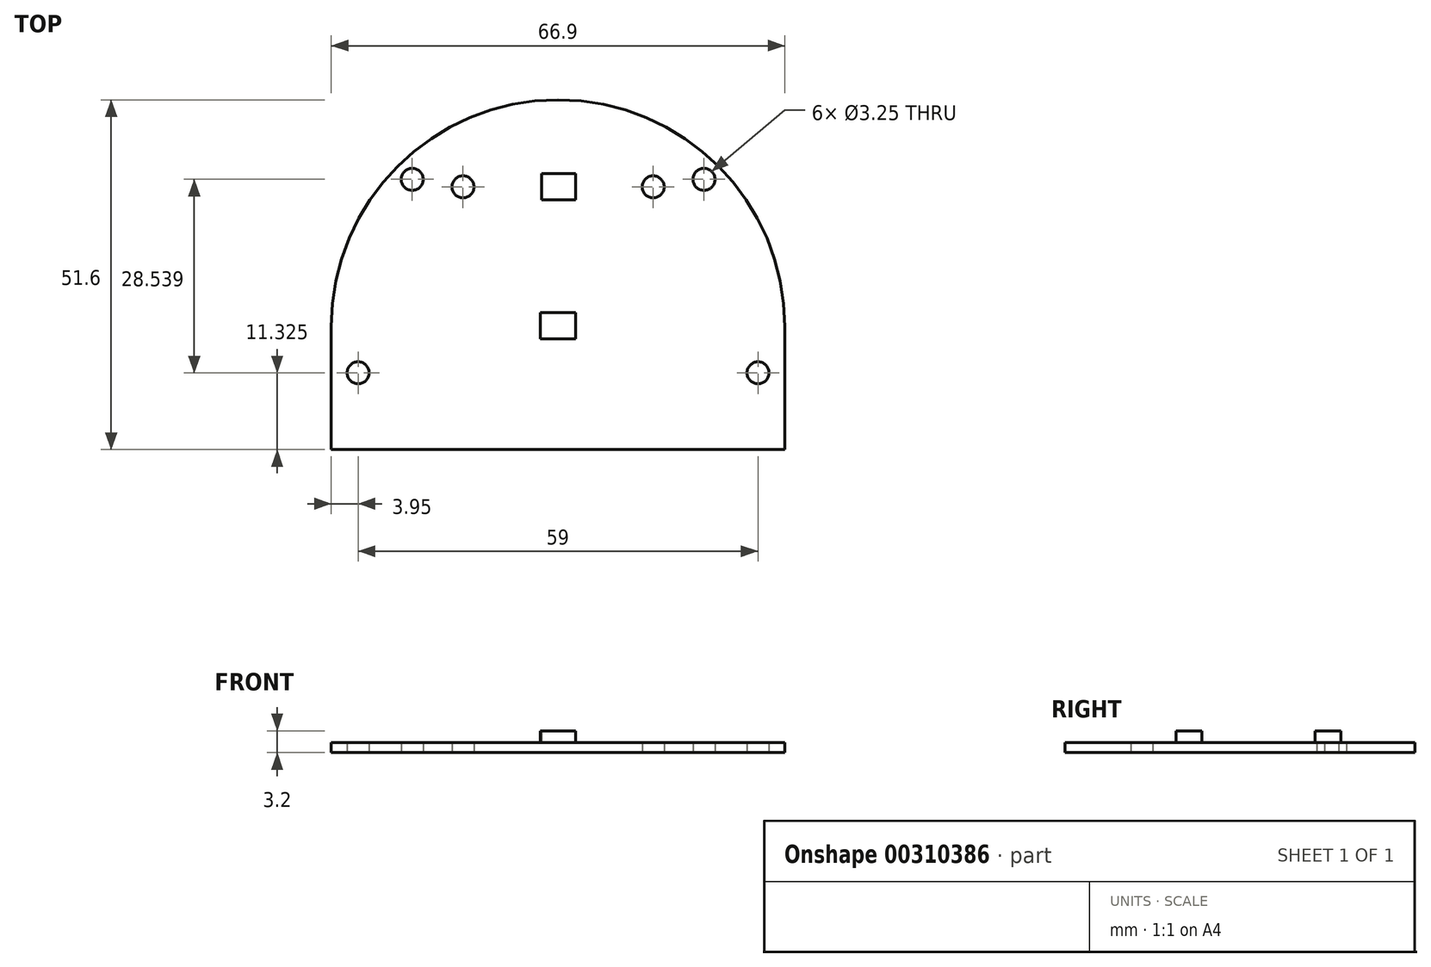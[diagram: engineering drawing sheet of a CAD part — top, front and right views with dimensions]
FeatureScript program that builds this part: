
annotation { "Feature Type Name" : "Feature", "Feature Type Description" : "" }
export const myFeature = defineFeature(function(context is Context, id is Id, definition is map)
    precondition{}
    {
        {
            var Q0;
            Q0=qCreatedBy(makeId("Top.planeOp"),FACE);
            var sketch = newSketch(context, id + "F0", { "sketchPlane" : qUnion([Q0])});
            skLineSegment(sketch, "E0.bottom", {"start": v(-33.45, 25.8) * mm, "end": v(33.45, 25.8) * mm});
            skLineSegment(sketch, "E0.top", {"start": v(-33.45, -25.8) * mm, "end": v(33.45, -25.8) * mm});
            skLineSegment(sketch, "E0.left", {"start": v(-33.45, 25.8) * mm, "end": v(-33.45, -25.8) * mm});
            skLineSegment(sketch, "E0.right", {"start": v(33.45, 25.8) * mm, "end": v(33.45, -25.8) * mm});
            skPoint(sketch, "E0.middle", {"position": v(0, 0) * mm});
            skSolve(sketch);
        }
        {
            var Q0;
            Q0=makeQuery(id+"F0.imprint","IMPRINT",FACE,{"disambiguationData":[TD([[makeQuery(id+"F0.imprint","IMPRINT",EDGE,{"derivedFrom":sQuery(id+"F0.wireOp",EDGE,"E0.bottom")}),-1.0]])]});
            extrude(context, id + "F1", {"entities" : qUnion([Q0]), "depth" : 1.5 * mm});
        }
        {
            var Q0;
            Q0=makeQuery(id+"F1.opExtrude","SWEPT_EDGE",EDGE,{"disambiguationData":[OSD([sQuery(id+"F0.wireOp",EDGE,"E0.bottom"),sQuery(id+"F0.wireOp",EDGE,"E0.left")])]});
            var Q1;
            Q1=makeQuery(id+"F1.opExtrude","SWEPT_EDGE",EDGE,{"disambiguationData":[OSD([sQuery(id+"F0.wireOp",EDGE,"E0.bottom"),sQuery(id+"F0.wireOp",EDGE,"E0.right")])]});
            fillet(context, id + "F2", {"entities" : qUnion([Q0, Q1]), "radius" : 33.45 * mm, "tangentPropagation" : true, "allowEdgeOverflow" : false});
        }
        {
            var Q0;
            Q0=qCreatedBy(makeId("Top.planeOp"),FACE);
            var sketch = newSketch(context, id + "F3", { "sketchPlane" : qUnion([Q0])});
            skCircle(sketch, "E1", {"center": v(-21.53, 14.06) * mm, "radius": 1.63 * mm});
            skCircle(sketch, "E2", {"center": v(-14.02, 12.95) * mm, "radius": 1.63 * mm});
            skCircle(sketch, "E3", {"center": v(21.53, 14.06) * mm, "radius": 1.63 * mm});
            skCircle(sketch, "E4", {"center": v(14.03, 12.95) * mm, "radius": 1.63 * mm});
            skCircle(sketch, "E5", {"center": v(-29.5, -14.48) * mm, "radius": 1.63 * mm});
            skCircle(sketch, "E6", {"center": v(29.5, -14.48) * mm, "radius": 1.63 * mm});
            skSolve(sketch);
        }
        {
            var Q0;
            Q0 = qSketchRegion(id + "F3", true);
            extrude(context, id + "F4", {"entities" : qUnion([Q0]), "operationType" : NewBodyOperationType.REMOVE, "depth" : 1.5 * mm});
        }
        {
            var Q0;
            Q0=makeQuery(id+"F1.opExtrude","CAP_FACE",FACE,{"disambiguationData":[OSD([sQuery(id+"F0.wireOp",EDGE,"E0.bottom"),sQuery(id+"F0.wireOp",EDGE,"E0.top"),sQuery(id+"F0.wireOp",EDGE,"E0.left"),sQuery(id+"F0.wireOp",EDGE,"E0.right")])],"isStart":false});
            var sketch = newSketch(context, id + "F5", { "sketchPlane" : qUnion([Q0])});
            skLineSegment(sketch, "E7.bottom", {"start": v(-2.6, -9.45) * mm, "end": v(2.6, -9.45) * mm});
            skLineSegment(sketch, "E7.top", {"start": v(-2.6, -5.6) * mm, "end": v(2.6, -5.6) * mm});
            skLineSegment(sketch, "E7.left", {"start": v(-2.6, -9.45) * mm, "end": v(-2.6, -5.6) * mm});
            skLineSegment(sketch, "E7.right", {"start": v(2.6, -9.45) * mm, "end": v(2.6, -5.6) * mm});
            skPoint(sketch, "E7.middle", {"position": v(0, -7.53) * mm});
            skLineSegment(sketch, "E8.bottom", {"start": v(-2.45, 11.05) * mm, "end": v(2.6, 11.05) * mm});
            skLineSegment(sketch, "E8.top", {"start": v(-2.45, 14.9) * mm, "end": v(2.6, 14.9) * mm});
            skLineSegment(sketch, "E8.left", {"start": v(-2.45, 11.05) * mm, "end": v(-2.45, 14.9) * mm});
            skLineSegment(sketch, "E8.right", {"start": v(2.6, 11.05) * mm, "end": v(2.6, 14.9) * mm});
            skPoint(sketch, "E8.middle", {"position": v(0.08, 12.97) * mm});
            skSolve(sketch);
        }
        {
            var Q0;
            Q0 = qSketchRegion(id + "F5", true);
            extrude(context, id + "F6", {"entities" : qUnion([Q0]), "operationType" : NewBodyOperationType.ADD, "depth" : 1.7 * mm});
        }
    });
